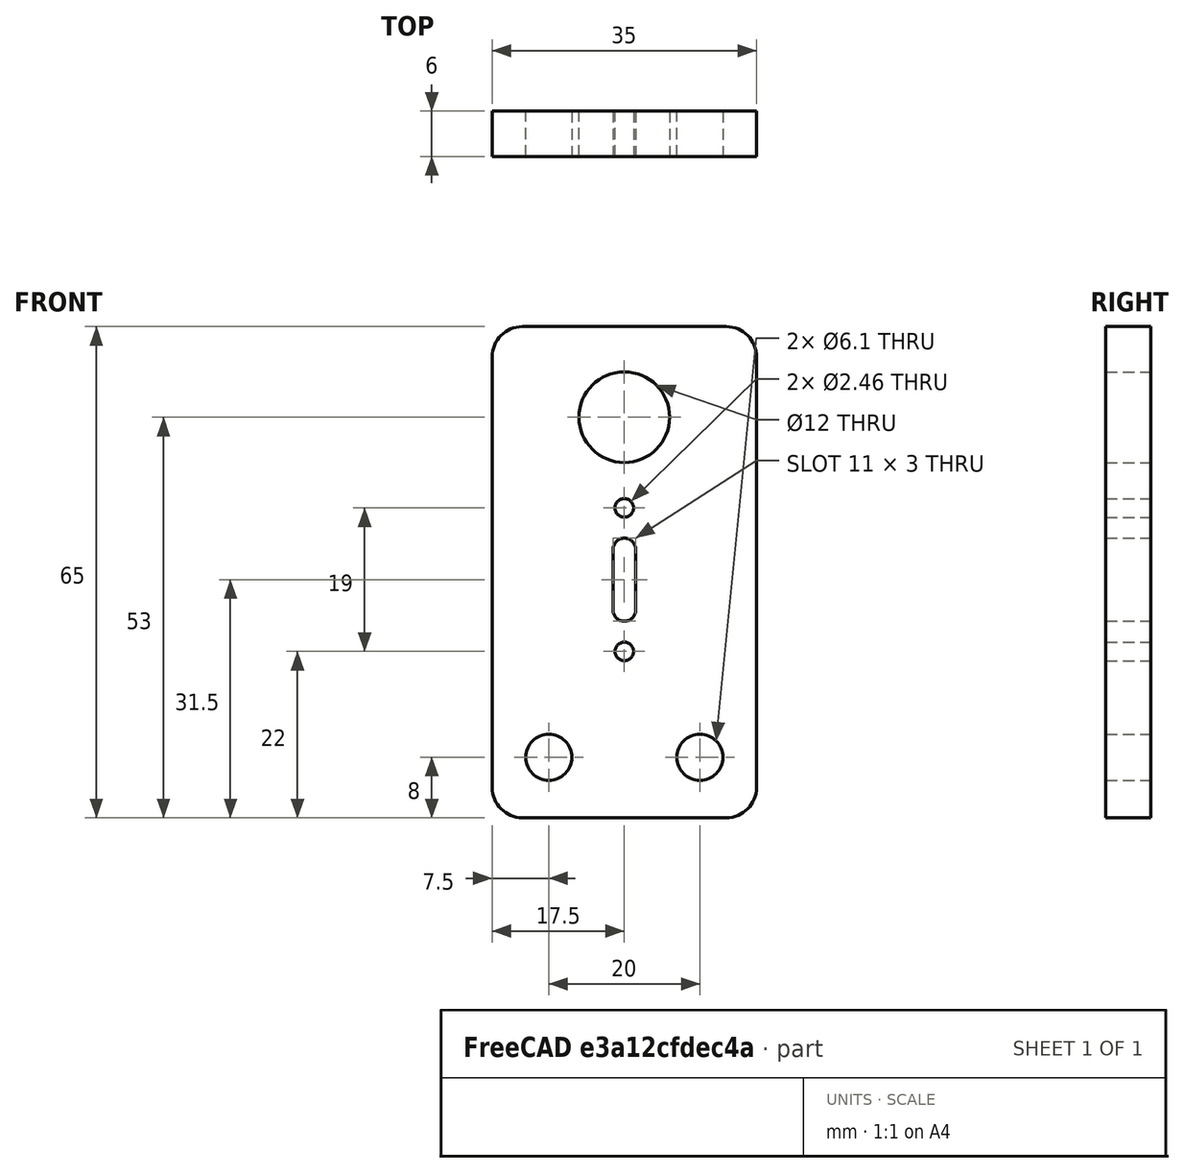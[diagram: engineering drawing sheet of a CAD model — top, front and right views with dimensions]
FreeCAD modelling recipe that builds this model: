
FCSTD DOCUMENT  (FreeCAD 0.15R4671 (Git))
Label: Plaque_support
License: All rights reserved
LicenseURL: http://en.wikipedia.org/wiki/All_rights_reserved
objects: Sketcher::SketchObject×1, PartDesign::Pad×1
note: 3 computed .brp shape members not serialized (recipe doc carries the construction recipe); baked Part::Feature solids carry a one-line shape summary decoded from their .brp

FEATURE [Sketcher::SketchObject] Sketch
  Placement = pos=(0,0,0) rot=(-1,0,0;4.71239rad)
  sketch-geometry (17):
    g0: Circle CenterX=0 CenterY=0 CenterZ=0 NormalX=0 NormalY=0 NormalZ=1 Radius=6
    g1: Circle CenterX=0 CenterY=-12 CenterZ=0 NormalX=0 NormalY=0 NormalZ=1 Radius=1.2295
    g2: Circle CenterX=0 CenterY=-31 CenterZ=0 NormalX=0 NormalY=0 NormalZ=1 Radius=1.2295
    g3: ArcOfCircle CenterX=0 CenterY=-17.5 CenterZ=0 NormalX=0 NormalY=0 NormalZ=1 Radius=1.5 StartAngle=0 EndAngle=3.14159
    g4: ArcOfCircle CenterX=0 CenterY=-25.5 CenterZ=0 NormalX=0 NormalY=0 NormalZ=1 Radius=1.5 StartAngle=3.14159 EndAngle=6.28319
    g5: LineSegment StartX=-1.5 StartY=-17.5 StartZ=0 EndX=-1.5 EndY=-25.5 EndZ=0
    g6: LineSegment StartX=1.5 StartY=-17.5 StartZ=0 EndX=1.5 EndY=-25.5 EndZ=0
    g7: Circle CenterX=-10 CenterY=-45 CenterZ=0 NormalX=0 NormalY=0 NormalZ=1 Radius=3.05
    g8: Circle CenterX=10 CenterY=-45 CenterZ=0 NormalX=0 NormalY=0 NormalZ=1 Radius=3.05
    g9: LineSegment StartX=-17.5 StartY=7.99998 StartZ=0 EndX=-17.5 EndY=-49 EndZ=0
    g10: ArcOfCircle CenterX=-13.5 CenterY=-49 CenterZ=0 NormalX=0 NormalY=0 NormalZ=1 Radius=4 StartAngle=3.14159 EndAngle=4.71239
    g11: LineSegment StartX=-13.5 StartY=-53 StartZ=0 EndX=13.5 EndY=-53 EndZ=0
    g12: ArcOfCircle CenterX=13.5 CenterY=-49 CenterZ=0 NormalX=0 NormalY=0 NormalZ=1 Radius=4 StartAngle=4.71239 EndAngle=6.28319
    g13: LineSegment StartX=17.5 StartY=-49 StartZ=0 EndX=17.5 EndY=8 EndZ=0
    g14: ArcOfCircle CenterX=13.5 CenterY=8 CenterZ=0 NormalX=0 NormalY=0 NormalZ=1 Radius=4 StartAngle=0 EndAngle=1.5708
    g15: LineSegment StartX=13.5 StartY=12 StartZ=0 EndX=-13.5 EndY=12 EndZ=0
    g16: ArcOfCircle CenterX=-13.5 CenterY=8 CenterZ=0 NormalX=0 NormalY=0 NormalZ=1 Radius=4 StartAngle=1.5708 EndAngle=3.1416
  constraints (44):
    c: Coincident(g0,g-1)
    c: Radius(g0) = 6
    c: PointOnObject(g1,g-2)
    c: PointOnObject(g2,g-2)
    c: Tangent(g3,g6) = 1.5708
    c: Tangent(g3,g5) = -1.5708
    c: Tangent(g5,g4) = -1.5708
    c: Tangent(g6,g4) = 1.5708
    c: Vertical(g5)
    c: Equal(g3,g4)
    c: Radius(g7) = 3.05
    c: Equal(g7,g8)
    c: DistanceX(g7,g8) = 20
    c: Symmetric(g7,g8,g-2)
    c: DistanceY(g-1,g7) = -45
    c: PointOnObject(g3,g-2)
    c: Radius(g3) = 1.5
    c: DistanceY(g-1,g1) = -12
    c: Radius(g1) = 1.2295
    c: Equal(g1,g2)
    c: DistanceY(g1,g3) = -5.5
    c: DistanceY(g3,g4) = -8
    c: DistanceY(g1,g2) = -19
    c: Vertical(g9)
    c: Tangent(g9,g10) = -1.5708
    c: Tangent(g10,g11) = -1.5708
    c: Tangent(g11,g12) = -1.5708
    c: Tangent(g12,g13) = -1.5708
    c: Tangent(g13,g14) = -1.5708
    c: Tangent(g14,g15) = -1.5708
    c: Tangent(g15,g16) = -1.5708
    c: Coincident(g16,g9)
    c: Tangent(g9,g16)
    c: Horizontal(g15)
    c: Horizontal(g11)
    c: Vertical(g13)
    c: Radius(g16) = 4
    c: Equal(g16,g14)
    c: Equal(g16,g12)
    c: Equal(g16,g10)
    c: DistanceY(g-1,g15) = 12
    c: Symmetric(g9,g13,g-2)
    c: DistanceY(g7,g10) = -8
    c: DistanceX(g9,g13) = 35
FEATURE [PartDesign::Pad] Pad
  Length = 6
  Length2 = 100
  Placement = pos=(0,0,0) rot=(-1,0,0;4.71239rad)
  Sketch = -> Sketch
  Type = 0
